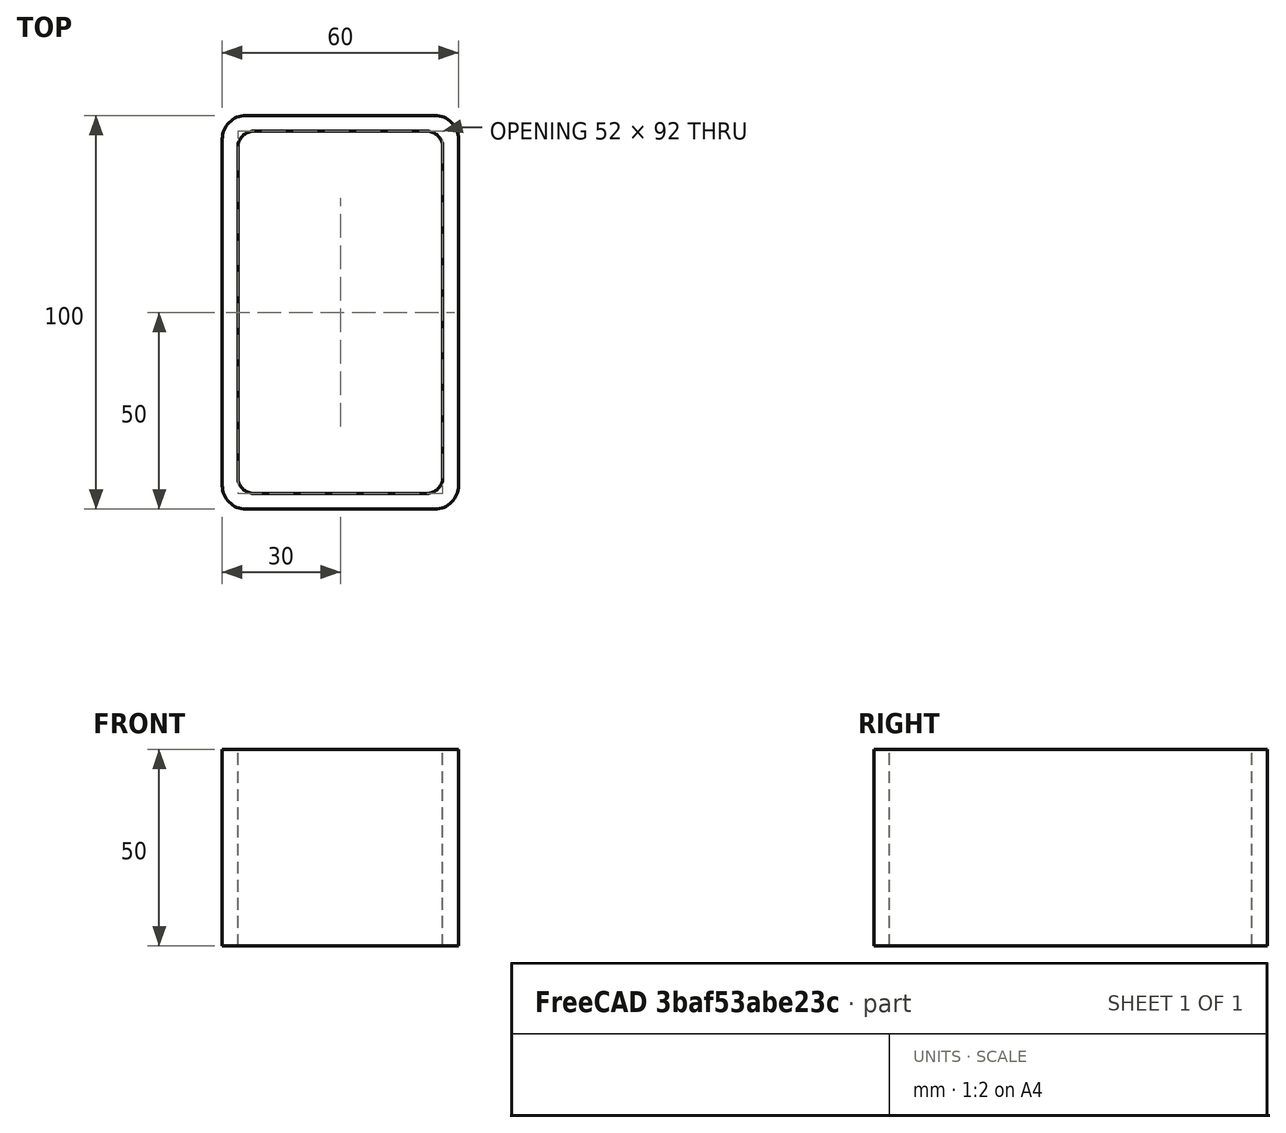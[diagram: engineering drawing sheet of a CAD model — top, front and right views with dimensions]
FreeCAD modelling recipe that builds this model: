
FCSTD DOCUMENT  (FreeCAD 0.15R4671 (Git))
Label: Rectangular hollow section 100x60x4 EN10219 S235JRH
License: All rights reserved
LicenseURL: http://en.wikipedia.org/wiki/All_rights_reserved
objects: Sketcher::SketchObject×1, Part::Extrusion×1
note: 2 computed .brp shape members not serialized (recipe doc carries the construction recipe); baked Part::Feature solids carry a one-line shape summary decoded from their .brp

FEATURE [Sketcher::SketchObject] Sketch
  sketch-geometry (16):
    g0: LineSegment StartX=-22 StartY=46 StartZ=0 EndX=22 EndY=46 EndZ=0
    g1: LineSegment StartX=26 StartY=42 StartZ=0 EndX=26 EndY=-42 EndZ=0
    g2: LineSegment StartX=22 StartY=-46 StartZ=0 EndX=-22 EndY=-46 EndZ=0
    g3: LineSegment StartX=-26 StartY=-42 StartZ=0 EndX=-26 EndY=42 EndZ=0
    g4: LineSegment StartX=-24 StartY=50 StartZ=0 EndX=24 EndY=50 EndZ=0
    g5: LineSegment StartX=30 StartY=44 StartZ=0 EndX=30 EndY=-44 EndZ=0
    g6: LineSegment StartX=24 StartY=-50 StartZ=0 EndX=-24 EndY=-50 EndZ=0
    g7: LineSegment StartX=-30 StartY=-44 StartZ=0 EndX=-30 EndY=44 EndZ=0
    g8: ArcOfCircle CenterX=-22 CenterY=42 CenterZ=0 NormalX=0 NormalY=0 NormalZ=1 Radius=4 StartAngle=1.5708 EndAngle=3.14159
    g9: ArcOfCircle CenterX=22 CenterY=42 CenterZ=0 NormalX=0 NormalY=0 NormalZ=1 Radius=4 StartAngle=0 EndAngle=1.5708
    g10: ArcOfCircle CenterX=22 CenterY=-42 CenterZ=0 NormalX=0 NormalY=0 NormalZ=1 Radius=4 StartAngle=4.71239 EndAngle=6.28319
    g11: ArcOfCircle CenterX=-22 CenterY=-42 CenterZ=0 NormalX=0 NormalY=0 NormalZ=1 Radius=4 StartAngle=3.14159 EndAngle=4.71239
    g12: ArcOfCircle CenterX=24 CenterY=44 CenterZ=0 NormalX=0 NormalY=0 NormalZ=1 Radius=6 StartAngle=0 EndAngle=1.5708
    g13: ArcOfCircle CenterX=24 CenterY=-44 CenterZ=0 NormalX=0 NormalY=0 NormalZ=1 Radius=6 StartAngle=4.71239 EndAngle=6.28319
    g14: ArcOfCircle CenterX=-24 CenterY=-44 CenterZ=0 NormalX=0 NormalY=0 NormalZ=1 Radius=6 StartAngle=3.14159 EndAngle=4.71239
    g15: ArcOfCircle CenterX=-24 CenterY=44 CenterZ=0 NormalX=0 NormalY=0 NormalZ=1 Radius=6 StartAngle=1.5708 EndAngle=3.14159
  constraints (36):
    c: Horizontal(g2)
    c: Vertical(g3)
    c: Horizontal(g6)
    c: Vertical(g7)
    c: Tangent(g3,g8) = 1.5708
    c: Tangent(g0,g8) = 1.5708
    c: Tangent(g0,g9) = 1.5708
    c: Tangent(g1,g9) = 1.5708
    c: Tangent(g1,g10) = 1.5708
    c: Tangent(g2,g10) = 1.5708
    c: Tangent(g2,g11) = 1.5708
    c: Tangent(g3,g11) = 1.5708
    c: Tangent(g4,g12) = 1.5708
    c: Tangent(g5,g12) = 1.5708
    c: Tangent(g5,g13) = 1.5708
    c: Tangent(g6,g13) = 1.5708
    c: Tangent(g6,g14) = 1.5708
    c: Tangent(g7,g14) = 1.5708
    c: Tangent(g7,g15) = 1.5708
    c: Tangent(g4,g15) = 1.5708
    c: Equal(g9,g8)
    c: Equal(g9,g11)
    c: Equal(g9,g10)
    c: Equal(g12,g15)
    c: Equal(g12,g14)
    c: Equal(g12,g13)
    c: Symmetric(g4,g6,g-1)
    c: Symmetric(g7,g5,g-2)
    c: DistanceY(g4,g6) = -100
    c: DistanceX(g7,g5) = 60
    c: Symmetric(g3,g1,g-2)
    c: Symmetric(g0,g2,g-1)
    c: DistanceY(g0,g4) = 4
    c: DistanceX(g5,g1) = -4
    c: Radius(g9) = 4
    c: Radius(g12) = 6
FEATURE [Part::Extrusion] Extrude  label="Rectangular hollow section 100x60x4 EN10219 S235JRH"
  Base = -> Sketch
  Dir = (0,0,50)
  Solid = true
